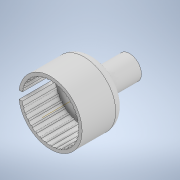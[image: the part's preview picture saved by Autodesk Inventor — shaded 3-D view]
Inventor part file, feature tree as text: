
AUTODESK INVENTOR PART (.ipt)
format: ipt  version: 2020 (Build 240168000, 168)  size: 264,192 bytes
history: native  units: in
note: dims shown in document units (in); Inventor stores cm internally (conversion verified against a paired STEP export)
features: extrude x8, sketch x8, fillet x1, other x1, pattern_circular x1
ambient origin geometry x8: Origin, YZ Plane, XZ Plane, XY Plane, X Axis, Y Axis, Z Axis, Center Point
bodies: Solid1 (feature_tree)
feature tree (19):
  extrude  "Extrusion1"  Depth=1.0in TaperAngle=0.0deg
  extrude  "Extrusion2"  Depth=0.42in TaperAngle=0.0deg
  extrude  "Extrusion3"  Depth=0.19in
  extrude  "Extrusion4"  Depth=0.45in
  fillet  "Fillet2"  Radius=0.45in
  extrude  "Extrusion6"  Depth=0.125in
  sketch  "Sketch7"  dims[d20=0.2in d21=0.05in]
  other  "Work Axis1"
  extrude  "Extrusion7"  Depth=0.05in
  pattern_circular  "Circular Pattern1"  [2 undecoded]
  extrude  "Extrusion8"  Depth=0.42in TaperAngle=360.0deg
  extrude  "Extrusion9"  Depth=0.42in TaperAngle=0.0deg
  sketch  "Sketch1"  dims[d0=0.8in d1=1.0in d2=0.0in]
  sketch  "Sketch2"  dims[d3=0.72in d4=0.42in d5=0.0in]
  sketch  "Sketch3"  dims[d6=0.21in d7=0.19in]
  sketch  "Sketch4"  dims[d8=0.45in d9=0.0in d10=0.3in d11=0.45in d12=0.0in]
  sketch  "Sketch6"  dims[d14=0.125in d19=0.1in]
  sketch  "Sketch8"  dims[d22=0.42in d23=0.0in]
  sketch  "Sketch9"  dims[d24=0.02in d25=0.42in d26=0.0in d27=13.7795in d28=360.0deg d30=0.42in d31=0.0in d32=0.42in d33=0.0in]
note: 2 required parameter values undecoded (feature->parameter linkage not recoverable at this tier; creation-order binding heuristic only, values carry confidence <= 0.55)
